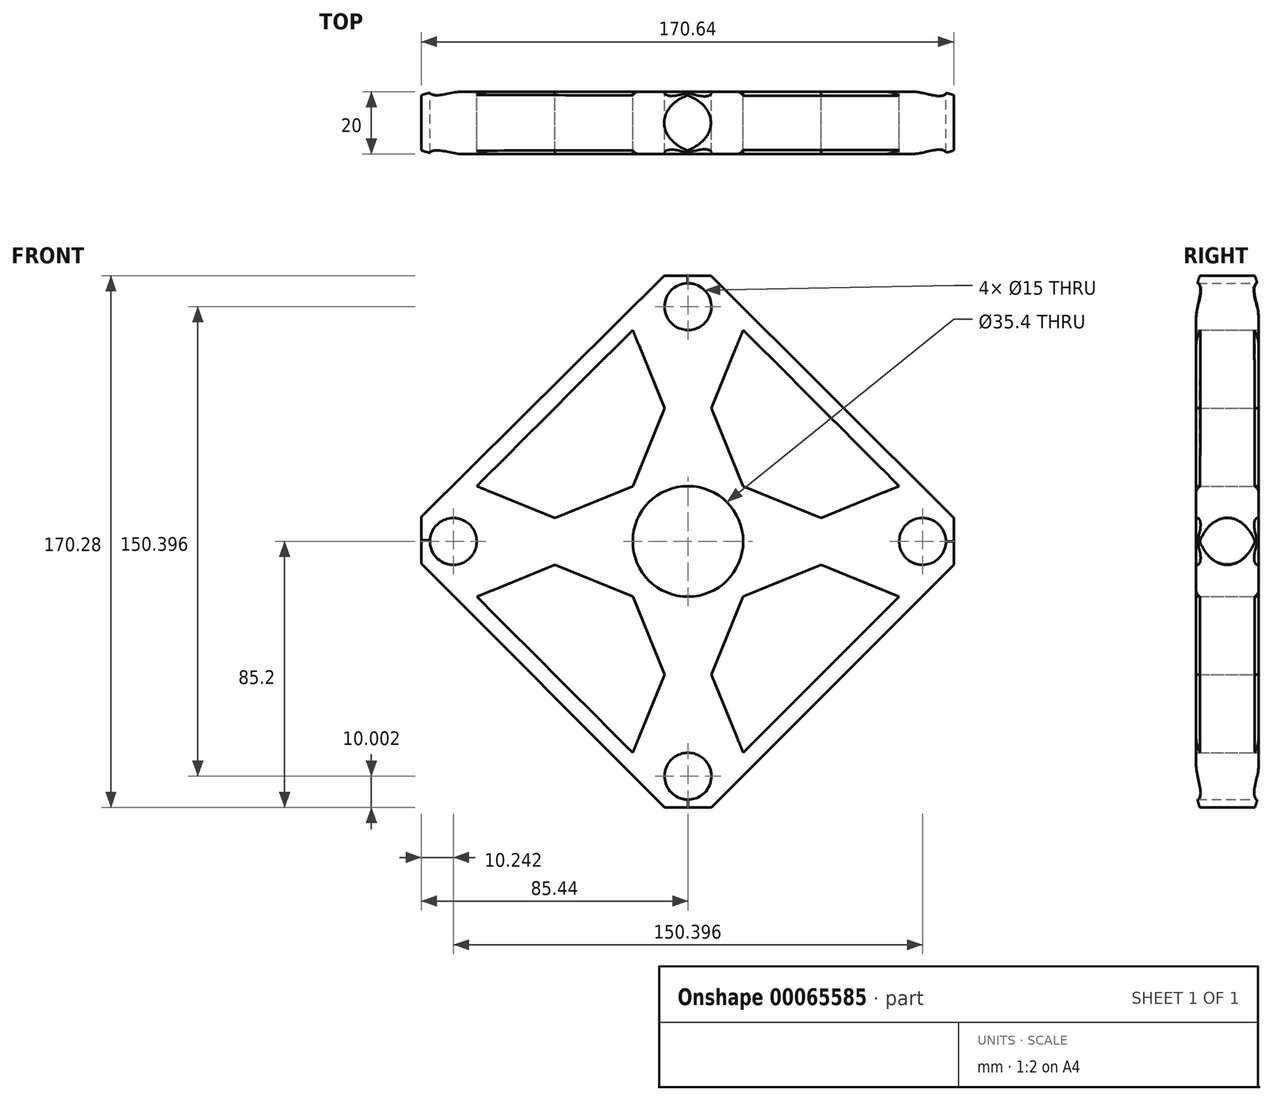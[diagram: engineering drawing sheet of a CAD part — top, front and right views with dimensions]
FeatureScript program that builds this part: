
annotation { "Feature Type Name" : "Feature", "Feature Type Description" : "" }
export const myFeature = defineFeature(function(context is Context, id is Id, definition is map)
    precondition{}
    {
        {
            var Q0;
            Q0=qCreatedBy(makeId("Front.planeOp"),FACE);
            var sketch = newSketch(context, id + "F0", { "sketchPlane" : qUnion([Q0])});
            skCircle(sketch, "E0", {"center": v(0, 0) * mm, "radius": 17.7 * mm});
            skCircle(sketch, "E1", {"center": v(0, 75.2) * mm, "radius": 7.5 * mm});
            skLineSegment(sketch, "E2", {"start": v(0, 67.7) * mm, "end": v(0, 17.7) * mm});
            skCircle(sketch, "E3", {"center": v(0, -75.2) * mm, "radius": 7.5 * mm});
            skCircle(sketch, "E4", {"center": v(-75.2, 0) * mm, "radius": 7.5 * mm});
            skLineSegment(sketch, "E5", {"start": v(-17.7, 0) * mm, "end": v(-67.7, 0) * mm});
            skCircle(sketch, "E6", {"center": v(75.2, 0) * mm, "radius": 7.5 * mm});
            skLineSegment(sketch, "E7", {"start": v(0, -67.7) * mm, "end": v(0, -31.68) * mm});
            skLineSegment(sketch, "E8", {"start": v(0, -17.7) * mm, "end": v(0, -31.68) * mm});
            skLineSegment(sketch, "E9", {"start": v(17.7, 0) * mm, "end": v(67.7, 0) * mm});
            skLineSegment(sketch, "E10", {"start": v(-7.65, 85.08) * mm, "end": v(7.35, 85.08) * mm});
            skLineSegment(sketch, "E11", {"start": v(-85.44, -7.16) * mm, "end": v(-85.44, 7.84) * mm});
            skLineSegment(sketch, "E12", {"start": v(-85.44, -7.16) * mm, "end": v(-75.45, -7.5) * mm});
            skLineSegment(sketch, "E13", {"start": v(-7.65, 85.08) * mm, "end": v(-7.5, 75.08) * mm});
            skLineSegment(sketch, "E14", {"start": v(-7.5, -75.2) * mm, "end": v(-7.5, -85.2) * mm});
            skLineSegment(sketch, "E15", {"start": v(-7.5, -85.2) * mm, "end": v(7.5, -85.2) * mm});
            skLineSegment(sketch, "E16", {"start": v(75.2, -7.5) * mm, "end": v(85.2, -7.5) * mm});
            skLineSegment(sketch, "E17", {"start": v(85.2, -7.5) * mm, "end": v(85.2, 7.5) * mm});
            skLineSegment(sketch, "E18", {"start": v(-7.5, -85.2) * mm, "end": v(-17.7, -67.7) * mm});
            skLineSegment(sketch, "E19", {"start": v(7.5, -85.2) * mm, "end": v(17.7, -67.7) * mm});
            skLineSegment(sketch, "E20", {"start": v(-85.44, 7.84) * mm, "end": v(-67.7, 17.7) * mm});
            skLineSegment(sketch, "E21", {"start": v(-85.44, -7.16) * mm, "end": v(-67.7, -17.7) * mm});
            skLineSegment(sketch, "E22", {"start": v(-7.65, 85.08) * mm, "end": v(-17.7, 67.7) * mm});
            skLineSegment(sketch, "E23", {"start": v(7.35, 85.08) * mm, "end": v(17.7, 67.7) * mm});
            skLineSegment(sketch, "E24", {"start": v(85.2, 7.5) * mm, "end": v(67.7, 17.7) * mm});
            skLineSegment(sketch, "E25", {"start": v(85.2, -7.5) * mm, "end": v(67.7, -17.7) * mm});
            skLineSegment(sketch, "E26", {"start": v(-67.7, 17.7) * mm, "end": v(-17.7, 17.7) * mm});
            skLineSegment(sketch, "E27", {"start": v(-67.7, -17.7) * mm, "end": v(-17.7, -17.7) * mm});
            skLineSegment(sketch, "E28", {"start": v(67.7, 17.7) * mm, "end": v(17.7, 17.7) * mm});
            skLineSegment(sketch, "E29", {"start": v(67.7, -17.7) * mm, "end": v(17.7, -17.7) * mm});
            skLineSegment(sketch, "E30", {"start": v(-17.7, 17.7) * mm, "end": v(-17.7, 67.7) * mm});
            skLineSegment(sketch, "E31", {"start": v(17.7, 17.7) * mm, "end": v(17.7, 67.7) * mm});
            skLineSegment(sketch, "E32", {"start": v(-17.7, -17.7) * mm, "end": v(-17.7, -67.7) * mm});
            skLineSegment(sketch, "E33", {"start": v(17.7, -17.7) * mm, "end": v(17.7, -67.7) * mm});
            skLineSegment(sketch, "E34", {"start": v(-67.7, 17.7) * mm, "end": v(-42.7, 7.5) * mm});
            skLineSegment(sketch, "E35", {"start": v(-42.7, 7.5) * mm, "end": v(-17.7, 17.7) * mm});
            skLineSegment(sketch, "E36", {"start": v(-67.7, -17.7) * mm, "end": v(-42.7, -7.5) * mm});
            skLineSegment(sketch, "E37", {"start": v(-42.7, -7.5) * mm, "end": v(-17.7, -17.7) * mm});
            skLineSegment(sketch, "E38", {"start": v(-17.7, 67.7) * mm, "end": v(-7.5, 42.7) * mm});
            skLineSegment(sketch, "E39", {"start": v(-7.5, 42.7) * mm, "end": v(-17.7, 17.7) * mm});
            skLineSegment(sketch, "E40", {"start": v(17.7, 67.7) * mm, "end": v(7.5, 42.7) * mm});
            skPoint(sketch, "E40.endSnap0", {"position": v(0, 42.7) * mm});
            skLineSegment(sketch, "E41", {"start": v(7.5, 42.7) * mm, "end": v(17.7, 17.7) * mm});
            skLineSegment(sketch, "E42", {"start": v(17.7, 17.7) * mm, "end": v(42.7, 7.5) * mm});
            skLineSegment(sketch, "E43", {"start": v(42.7, 7.5) * mm, "end": v(67.7, 17.7) * mm});
            skLineSegment(sketch, "E44", {"start": v(17.7, -17.7) * mm, "end": v(42.7, -7.5) * mm});
            skLineSegment(sketch, "E45", {"start": v(42.7, -7.5) * mm, "end": v(67.7, -17.7) * mm});
            skLineSegment(sketch, "E46", {"start": v(-17.7, -17.7) * mm, "end": v(-7.5, -42.7) * mm});
            skLineSegment(sketch, "E47", {"start": v(-7.5, -42.7) * mm, "end": v(-17.7, -67.7) * mm});
            skLineSegment(sketch, "E48", {"start": v(17.7, -17.7) * mm, "end": v(7.5, -42.7) * mm});
            skLineSegment(sketch, "E49", {"start": v(7.5, -42.7) * mm, "end": v(17.7, -67.7) * mm});
            skLineSegment(sketch, "E50", {"start": v(-85.44, 7.84) * mm, "end": v(-7.65, 85.08) * mm});
            skLineSegment(sketch, "E51", {"start": v(-67.7, 17.7) * mm, "end": v(-17.7, 67.7) * mm});
            skLineSegment(sketch, "E52", {"start": v(67.7, 17.7) * mm, "end": v(17.7, 67.7) * mm});
            skLineSegment(sketch, "E53", {"start": v(85.2, 7.5) * mm, "end": v(7.35, 85.08) * mm});
            skLineSegment(sketch, "E54", {"start": v(85.2, -7.5) * mm, "end": v(7.5, -85.2) * mm});
            skLineSegment(sketch, "E55", {"start": v(17.7, -67.7) * mm, "end": v(67.7, -17.7) * mm});
            skLineSegment(sketch, "E56", {"start": v(-7.5, -85.2) * mm, "end": v(-85.44, -7.16) * mm});
            skLineSegment(sketch, "E57", {"start": v(-67.7, -17.7) * mm, "end": v(-17.7, -67.7) * mm});
            skSolve(sketch);
        }
        {
            var Q0;
            {var subQ3=sQuery(id+"F0.wireOp",EDGE,"E2");Q0=makeQuery(id+"F0.imprint","IMPRINT",FACE,{"disambiguationData":[TD([[makeQuery(id+"F0.imprint","IMPRINT",EDGE,{"derivedFrom":subQ3}),-1.0]])]});}
            var Q1;
            {var subQ4=sQuery(id+"F0.wireOp",EDGE,"E5");Q1=makeQuery(id+"F0.imprint","IMPRINT",FACE,{"disambiguationData":[TD([[makeQuery(id+"F0.imprint","IMPRINT",EDGE,{"derivedFrom":subQ4}),1.0]])]});}
            var Q2;
            {var subQ2=sQuery(id+"F0.wireOp",EDGE,"E7");Q2=makeQuery(id+"F0.imprint","IMPRINT",FACE,{"disambiguationData":[TD([[makeQuery(id+"F0.imprint","IMPRINT",EDGE,{"derivedFrom":subQ2}),-1.0]])]});}
            var Q3;
            {var subQ4=sQuery(id+"F0.wireOp",EDGE,"E2");Q3=makeQuery(id+"F0.imprint","IMPRINT",FACE,{"disambiguationData":[TD([[makeQuery(id+"F0.imprint","IMPRINT",EDGE,{"derivedFrom":subQ4}),1.0]])]});}
            var Q4;
            Q4=makeQuery(id+"F0.imprint","IMPRINT",FACE,{"disambiguationData":[TD([[makeQuery(id+"F0.imprint","IMPRINT",EDGE,{"derivedFrom":sQuery(id+"F0.wireOp",EDGE,"E23")}),1.0]])]});
            var Q5;
            Q5=makeQuery(id+"F0.imprint","IMPRINT",FACE,{"disambiguationData":[TD([[makeQuery(id+"F0.imprint","IMPRINT",EDGE,{"derivedFrom":sQuery(id+"F0.wireOp",EDGE,"E20")}),1.0]])]});
            var Q6;
            Q6=makeQuery(id+"F0.imprint","IMPRINT",FACE,{"disambiguationData":[TD([[makeQuery(id+"F0.imprint","IMPRINT",EDGE,{"derivedFrom":sQuery(id+"F0.wireOp",EDGE,"E18")}),1.0]])]});
            var Q7;
            Q7=makeQuery(id+"F0.imprint","IMPRINT",FACE,{"disambiguationData":[TD([[makeQuery(id+"F0.imprint","IMPRINT",EDGE,{"derivedFrom":sQuery(id+"F0.wireOp",EDGE,"E19")}),-1.0]])]});
            extrude(context, id + "F1", {"entities" : qUnion([Q0, Q1, Q2, Q3, Q4, Q5, Q6, Q7]), "depth" : 20 * mm});
        }
        {
            var Q0;
            Q0=makeQuery(id+"F1.opExtrude","CAP_EDGE",EDGE,{"disambiguationData":[OSD([sQuery(id+"F0.wireOp",EDGE,"E53")])],"isStart":false});
            var Q1;
            Q1=makeQuery(id+"F1.opExtrude","CAP_EDGE",EDGE,{"disambiguationData":[OSD([sQuery(id+"F0.wireOp",EDGE,"E50")])],"isStart":false});
            var Q2;
            Q2=makeQuery(id+"F1.opExtrude","CAP_EDGE",EDGE,{"disambiguationData":[OSD([sQuery(id+"F0.wireOp",EDGE,"E56")])],"isStart":false});
            var Q3;
            Q3=makeQuery(id+"F1.opExtrude","CAP_EDGE",EDGE,{"disambiguationData":[OSD([sQuery(id+"F0.wireOp",EDGE,"E54")])],"isStart":false});
            fillet(context, id + "F2", {"entities" : qUnion([Q0, Q1, Q2, Q3]), "radius" : 10 * mm, "tangentPropagation" : true, "allowEdgeOverflow" : false});
        }
        {
            var Q0;
            Q0=makeQuery(id+"F1.opExtrude","CAP_EDGE",EDGE,{"disambiguationData":[OSD([sQuery(id+"F0.wireOp",EDGE,"E56")])],"isStart":true});
            var Q1;
            Q1=makeQuery(id+"F1.opExtrude","CAP_EDGE",EDGE,{"disambiguationData":[OSD([sQuery(id+"F0.wireOp",EDGE,"E54")])],"isStart":true});
            var Q2;
            Q2=makeQuery(id+"F1.opExtrude","CAP_EDGE",EDGE,{"disambiguationData":[OSD([sQuery(id+"F0.wireOp",EDGE,"E50")])],"isStart":true});
            var Q3;
            Q3=makeQuery(id+"F1.opExtrude","CAP_EDGE",EDGE,{"disambiguationData":[OSD([sQuery(id+"F0.wireOp",EDGE,"E53")])],"isStart":true});
            fillet(context, id + "F3", {"entities" : qUnion([Q0, Q1, Q2, Q3]), "radius" : 10 * mm, "tangentPropagation" : true, "allowEdgeOverflow" : false});
        }
    });
